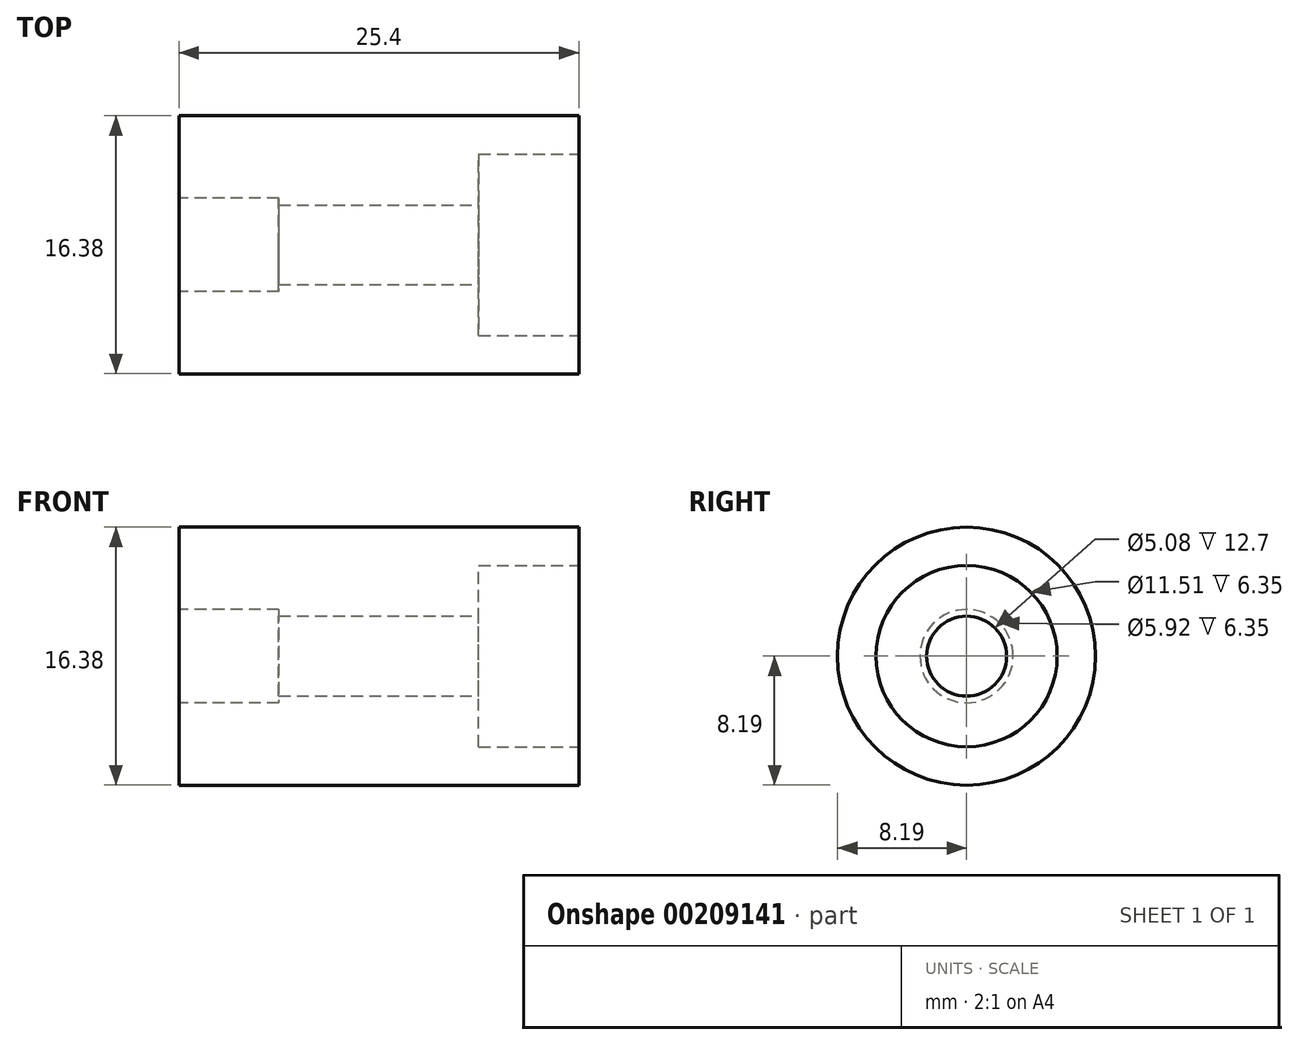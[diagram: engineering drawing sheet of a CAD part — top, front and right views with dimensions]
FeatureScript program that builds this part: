
annotation { "Feature Type Name" : "Feature", "Feature Type Description" : "" }
export const myFeature = defineFeature(function(context is Context, id is Id, definition is map)
    precondition{}
    {
        {
            var Q0;
            Q0=qCreatedBy(makeId("Right.planeOp"),FACE);
            var sketch = newSketch(context, id + "F0", { "sketchPlane" : qUnion([Q0])});
            skCircle(sketch, "E0", {"center": v(0, 0) * mm, "radius": 8.2 * mm});
            skSolve(sketch);
        }
        {
            var Q0;
            Q0=makeQuery(id+"F0.imprint","IMPRINT",FACE,{"disambiguationData":[TD([[makeQuery(id+"F0.imprint","IMPRINT",EDGE,{"derivedFrom":sQuery(id+"F0.wireOp",EDGE,"E0")}),1.0]])]});
            extrude(context, id + "F1", {"entities" : qUnion([Q0]), "depth" : 25.4 * mm});
        }
        {
            var Q0;
            Q0=makeQuery(id+"F1.opExtrude","CAP_FACE",FACE,{"disambiguationData":[OSD([sQuery(id+"F0.wireOp",EDGE,"E0")])],"isStart":false});
            var sketch = newSketch(context, id + "F2", { "sketchPlane" : qUnion([Q0])});
            skCircle(sketch, "E1", {"center": v(0, 0) * mm, "radius": 5.75 * mm});
            skSolve(sketch);
        }
        {
            var Q0;
            Q0=makeQuery(id+"F2.imprint","IMPRINT",FACE,{"disambiguationData":[TD([[makeQuery(id+"F2.imprint","IMPRINT",EDGE,{"derivedFrom":sQuery(id+"F2.wireOp",EDGE,"E1")}),1.0]])]});
            extrude(context, id + "F3", {"entities" : qUnion([Q0]), "operationType" : NewBodyOperationType.REMOVE, "oppositeDirection" : true, "depth" : 6.35 * mm});
        }
        {
            var Q0;
            Q0=makeQuery(id+"F3.boolean.opBoolean","COPY",FACE,{"derivedFrom":makeQuery(id+"F3.opExtrude","CAP_FACE",FACE,{"disambiguationData":[OSD([sQuery(id+"F2.wireOp",EDGE,"E1")])],"isStart":false})});
            var sketch = newSketch(context, id + "F4", { "sketchPlane" : qUnion([Q0])});
            skCircle(sketch, "E2", {"center": v(0, 0) * mm, "radius": 2.54 * mm});
            skSolve(sketch);
        }
        {
            var Q0;
            Q0=makeQuery(id+"F4.imprint","IMPRINT",FACE,{"disambiguationData":[TD([[makeQuery(id+"F4.imprint","IMPRINT",EDGE,{"derivedFrom":sQuery(id+"F4.wireOp",EDGE,"E2")}),1.0]])]});
            var Q1;
            Q1=sQuery(id+"F4.wireOp",EDGE,"E2");
            extrude(context, id + "F5", {"entities" : qUnion([Q0]), "operationType" : NewBodyOperationType.REMOVE, "surfaceEntities" : qUnion([Q1]), "endBound" : BoundingType.THROUGH_ALL, "oppositeDirection" : true, "depth" : 25.4 * mm});
        }
        {
            var Q0;
            Q0=makeQuery(id+"F1.opExtrude","CAP_FACE",FACE,{"disambiguationData":[OSD([sQuery(id+"F0.wireOp",EDGE,"E0")])],"isStart":true});
            var sketch = newSketch(context, id + "F6", { "sketchPlane" : qUnion([Q0])});
            skCircle(sketch, "E3", {"center": v(0, 0) * mm, "radius": 2.96 * mm});
            skSolve(sketch);
        }
        {
            var Q0;
            Q0=makeQuery(id+"F6.imprint","IMPRINT",FACE,{"disambiguationData":[TD([[makeQuery(id+"F6.imprint","IMPRINT",EDGE,{"derivedFrom":sQuery(id+"F6.wireOp",EDGE,"E3")}),1.0]])]});
            extrude(context, id + "F7", {"entities" : qUnion([Q0]), "operationType" : NewBodyOperationType.REMOVE, "oppositeDirection" : true, "depth" : 6.35 * mm});
        }
    });
